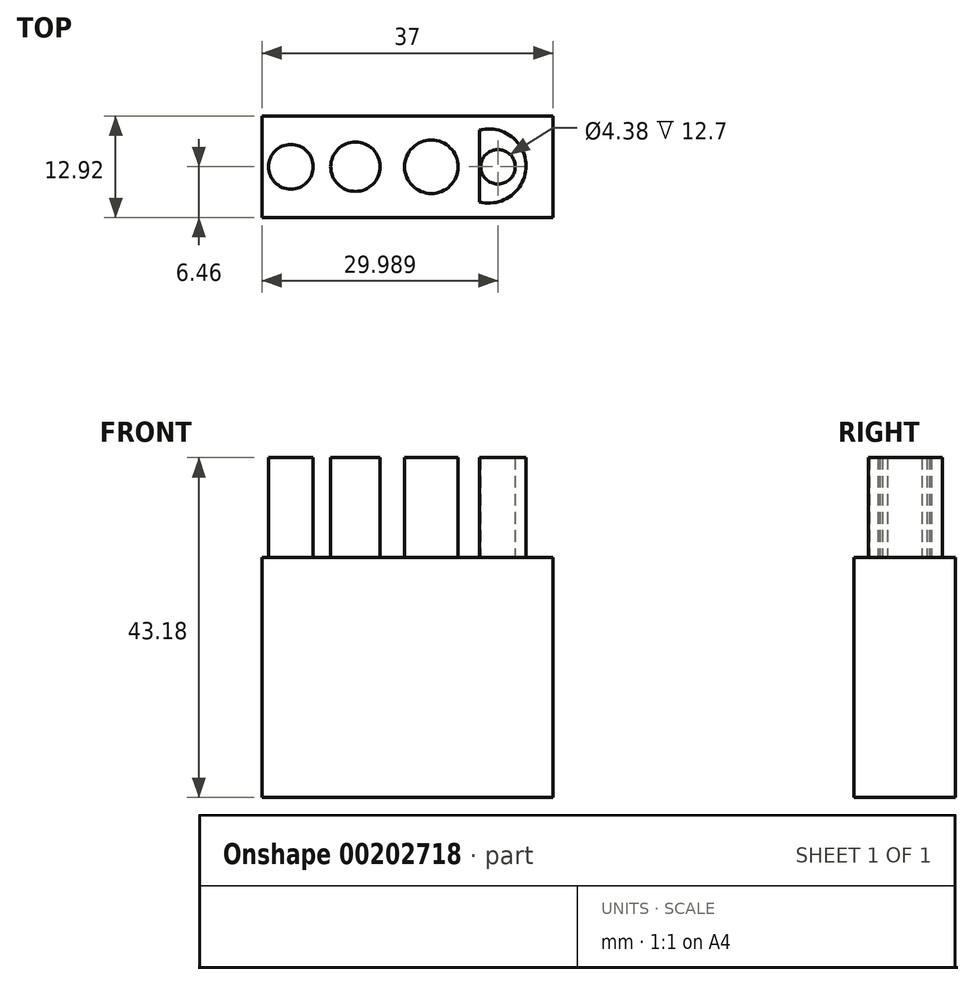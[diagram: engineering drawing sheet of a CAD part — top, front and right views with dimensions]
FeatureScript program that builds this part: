
annotation { "Feature Type Name" : "Feature", "Feature Type Description" : "" }
export const myFeature = defineFeature(function(context is Context, id is Id, definition is map)
    precondition{}
    {
        {
            var Q0;
            Q0=qCreatedBy(makeId("Top.planeOp"),FACE);
            var sketch = newSketch(context, id + "F0", { "sketchPlane" : qUnion([Q0])});
            skLineSegment(sketch, "E0.bottom", {"start": v(18.5, 6.46) * mm, "end": v(-18.5, 6.46) * mm});
            skLineSegment(sketch, "E0.top", {"start": v(18.5, -6.46) * mm, "end": v(-18.5, -6.46) * mm});
            skLineSegment(sketch, "E0.left", {"start": v(18.5, 6.46) * mm, "end": v(18.5, -6.46) * mm});
            skLineSegment(sketch, "E0.right", {"start": v(-18.5, 6.46) * mm, "end": v(-18.5, -6.46) * mm});
            skPoint(sketch, "E0.middle", {"position": v(0, 0) * mm});
            skSolve(sketch);
        }
        {
            var Q0;
            Q0=makeQuery(id+"F0.imprint","IMPRINT",FACE,{"disambiguationData":[TD([[makeQuery(id+"F0.imprint","IMPRINT",EDGE,{"derivedFrom":sQuery(id+"F0.wireOp",EDGE,"E0.bottom")}),1.0]])]});
            extrude(context, id + "F1", {"entities" : qUnion([Q0]), "depth" : 30.48 * mm});
        }
        {
            var Q0;
            Q0=makeQuery(id+"F1.opExtrude","CAP_FACE",FACE,{"disambiguationData":[OSD([sQuery(id+"F0.wireOp",EDGE,"E0.bottom"),sQuery(id+"F0.wireOp",EDGE,"E0.top"),sQuery(id+"F0.wireOp",EDGE,"E0.left"),sQuery(id+"F0.wireOp",EDGE,"E0.right")])],"isStart":false});
            var sketch = newSketch(context, id + "F2", { "sketchPlane" : qUnion([Q0])});
            skCircle(sketch, "E1", {"center": v(-14.82, 0) * mm, "radius": 2.84 * mm});
            skCircle(sketch, "E2", {"center": v(-6.62, 0) * mm, "radius": 3.14 * mm});
            skCircle(sketch, "E3", {"center": v(3.02, 0) * mm, "radius": 3.4 * mm});
            skLineSegment(sketch, "E4", {"start": v(9.12, 0) * mm, "end": v(9.12, 4.65) * mm});
            skLineSegment(sketch, "E5", {"start": v(9.12, 0) * mm, "end": v(9.12, -4.46) * mm});
            skArc(sketch, "E6", {"start": v(9.12, -4.46) * mm, "mid": v(15.04, 0.1) * mm, "end": v(9.12, 4.65) * mm});
            skCircle(sketch, "E7", {"center": v(11.49, 0) * mm, "radius": 2.2 * mm});
            skCircle(sketch, "E8", {"center": v(11.49, 0) * mm, "radius": 1.56 * mm});
            skSolve(sketch);
        }
        {
            var Q0;
            Q0 = qSketchRegion(id + "F2", true);
            extrude(context, id + "F3", {"entities" : qUnion([Q0]), "operationType" : NewBodyOperationType.ADD, "depth" : 12.7 * mm});
        }
    });
